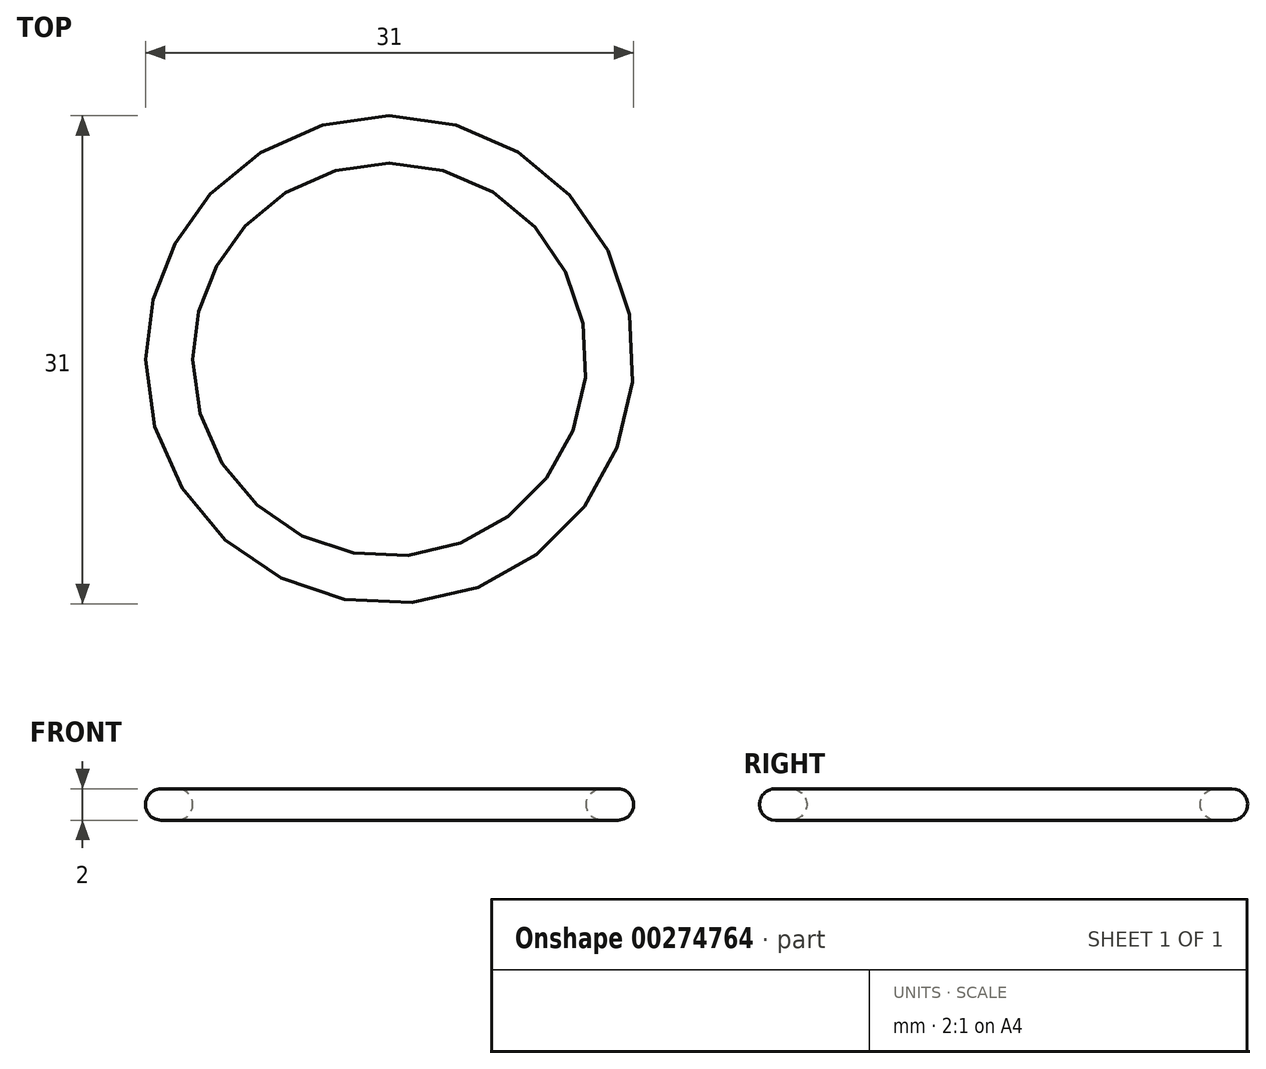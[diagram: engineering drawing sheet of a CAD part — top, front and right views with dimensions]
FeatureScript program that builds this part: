
annotation { "Feature Type Name" : "Feature", "Feature Type Description" : "" }
export const myFeature = defineFeature(function(context is Context, id is Id, definition is map)
    precondition{}
    {
        {
            var Q0;
            Q0=qCreatedBy(makeId("Front.planeOp"),FACE);
            var sketch = newSketch(context, id + "F0", { "sketchPlane" : qUnion([Q0])});
            skLineSegment(sketch, "E0", {"start": v(13.5, 1) * mm, "end": v(14.5, 1) * mm});
            skLineSegment(sketch, "E1", {"start": v(14.5, -1) * mm, "end": v(13.5, -1) * mm});
            skArc(sketch, "E2", {"start": v(14.5, -1) * mm, "mid": v(15.5, 0) * mm, "end": v(14.5, 1) * mm});
            skArc(sketch, "E3", {"start": v(13.5, 1) * mm, "mid": v(12.5, 0) * mm, "end": v(13.5, -1) * mm});
            skLineSegment(sketch, "E4", {"start": v(14.5, 0) * mm, "end": v(13.5, 0) * mm, "construction": true});
            skLineSegment(sketch, "E5", {"start": v(13.5, 0) * mm, "end": v(0, 0) * mm, "construction": true});
            skLineSegment(sketch, "E6", {"start": v(0, 0) * mm, "end": v(0, 9.13) * mm, "construction": true});
            skSolve(sketch);
        }
        {
            var Q0;
            Q0 = qSketchRegion(id + "F0", true);
            var Q1;
            Q1=sQuery(id+"F0.wireOp",EDGE,"E6");
            revolve(context, id + "F1", {"entities" : qUnion([Q0]), "axis" : qUnion([Q1]), "revolveType" : RevolveType.FULL});
        }
    });
